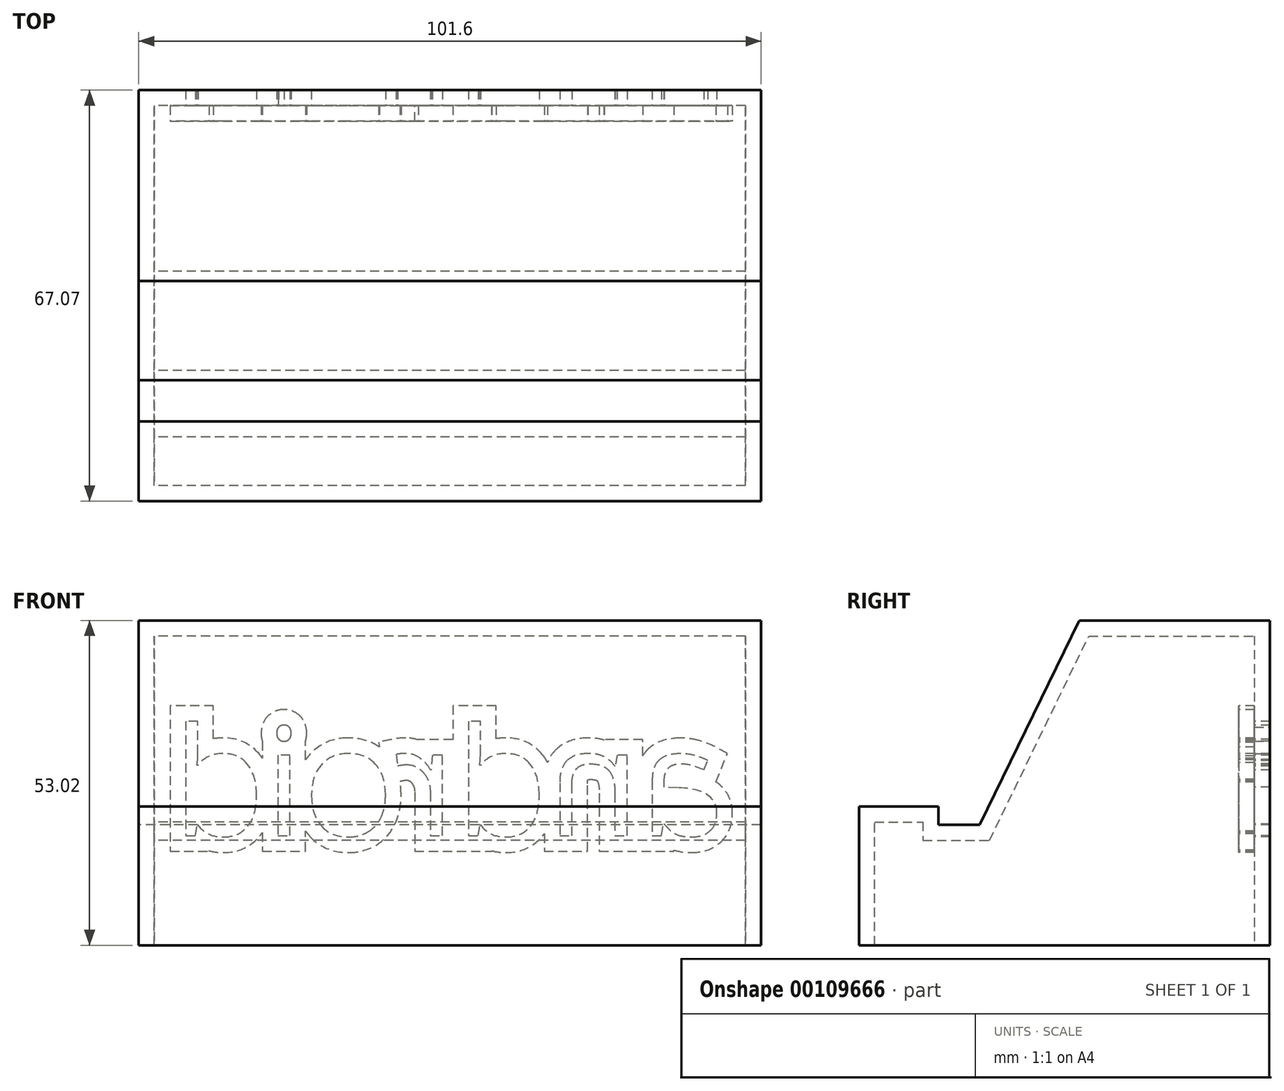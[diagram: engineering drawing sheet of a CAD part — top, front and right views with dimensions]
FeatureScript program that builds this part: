
annotation { "Feature Type Name" : "Feature", "Feature Type Description" : "" }
export const myFeature = defineFeature(function(context is Context, id is Id, definition is map)
    precondition{}
    {
        {
            var Q0;
            Q0=qCreatedBy(makeId("Right.planeOp"),FACE);
            var sketch = newSketch(context, id + "F0", { "sketchPlane" : qUnion([Q0])});
            skLineSegment(sketch, "E0", {"start": v(-84.53, -43.16) * mm, "end": v(-84.53, -20.49) * mm});
            skLineSegment(sketch, "E1", {"start": v(-84.53, -20.49) * mm, "end": v(-81.07, -20.49) * mm});
            skLineSegment(sketch, "E2", {"start": v(-81.07, -20.49) * mm, "end": v(-71.56, -20.49) * mm});
            skLineSegment(sketch, "E3", {"start": v(-71.56, -20.49) * mm, "end": v(-71.56, -23.5) * mm});
            skLineSegment(sketch, "E4", {"start": v(-71.56, -23.5) * mm, "end": v(-64.83, -23.5) * mm});
            skLineSegment(sketch, "E5", {"start": v(-64.83, -23.5) * mm, "end": v(-48.63, 9.86) * mm});
            skLineSegment(sketch, "E6", {"start": v(-48.63, 9.86) * mm, "end": v(-20, 9.86) * mm});
            skLineSegment(sketch, "E7", {"start": v(-20, 9.86) * mm, "end": v(-20, -43.16) * mm});
            skLineSegment(sketch, "E8", {"start": v(-20, -43.16) * mm, "end": v(-84.53, -43.16) * mm});
            skSolve(sketch);
        }
        {
            var Q0;
            Q0=makeQuery(id+"F0.imprint","IMPRINT",FACE,{"disambiguationData":[TD([[makeQuery(id+"F0.imprint","IMPRINT",EDGE,{"derivedFrom":sQuery(id+"F0.wireOp",EDGE,"E0")}),-1.0]])]});
            extrude(context, id + "F1", {"entities" : qUnion([Q0]), "depth" : 101.6 * mm});
        }
        {
            var Q0;
            Q0=makeQuery(id+"F1.opExtrude","SWEPT_FACE",FACE,{"disambiguationData":[OSD([sQuery(id+"F0.wireOp",EDGE,"E7")])]});
            var sketch = newSketch(context, id + "F2", { "sketchPlane" : qUnion([Q0])});
            skText(sketch, "E9", { "text": "android", "fontName": "OpenSans-Regular.ttf"});
            const initialGuessF2  = {"E9": [-0.0955, -0.02525, 1, 0, 0.01769]};
            skSetInitialGuess(sketch, initialGuessF2);
            skSolve(sketch);
        }
        {
            var Q0;
            Q0=makeQuery(id+"F2.imprint","IMPRINT",FACE,{"disambiguationData":[TD([[makeQuery(id+"F2.imprint","IMPRINT",EDGE,{"derivedFrom":sQuery(id+"F2.wireOp",EDGE,"E9.sketch_text.stroke-0")}),1.0]])]});
            extrude(context, id + "F3", {"entities" : qUnion([Q0]), "operationType" : NewBodyOperationType.ADD, "depth" : 2.54 * mm});
        }
        {
            var Q0;
            {var subQ0=sQuery(id+"F0.wireOp",EDGE,"E8");Q0=makeQuery(id+"F3.boolean.opBoolean","MERGE",FACE,{"derivedFrom":[makeQuery(id+"F1.opExtrude","SWEPT_FACE",FACE,{"disambiguationData":[OSD([subQ0])]}),makeQuery(id+"F3.opExtrude","SWEPT_FACE",FACE,{"disambiguationData":[OSD([sQuery(id+"F0.wireOp",EDGE,"E7"),subQ0])]})]});}
            shell(context, id + "F4", {"entities" : qUnion([Q0]), "thickness" : 2.54 * mm});
        }
    });
